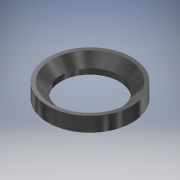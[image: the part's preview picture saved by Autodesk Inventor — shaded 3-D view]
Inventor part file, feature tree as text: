
AUTODESK INVENTOR PART (.ipt)
format: ipt  version: 2018 (Build 220112000, 112)  size: 144,896 bytes
history: native  units: mm (DEFAULTED — no unit token found)
features: sketch x2, extrude x1, hole x1, chamfer x1
ambient origin geometry x8: Origin, YZ Plane, XZ Plane, XY Plane, X Axis, Y Axis, Z Axis, Center Point
bodies: Solid1 (feature_tree)
feature tree (5):
  extrude  "Extrusion1"  Depth=8.0mm TaperAngle=0.0deg
  hole  "Hole1"  [1 undecoded]
  chamfer  "Chamfer1"  Angle=45.0deg  [1 undecoded]
  sketch  "Sketch1"  dims[d0=46.0mm d1=8.0mm d2=0.0mm]
  sketch  "Sketch3"  dims[d3=32.0mm d4=6.0mm d5=4.0mm d6=2.0mm d7=14.3117mm d8=8.0mm d9=20.594885mm d10=5.0mm d11=2.0mm d12=45.0deg]
note: 2 required parameter values undecoded (feature->parameter linkage not recoverable at this tier; creation-order binding heuristic only, values carry confidence <= 0.55)
